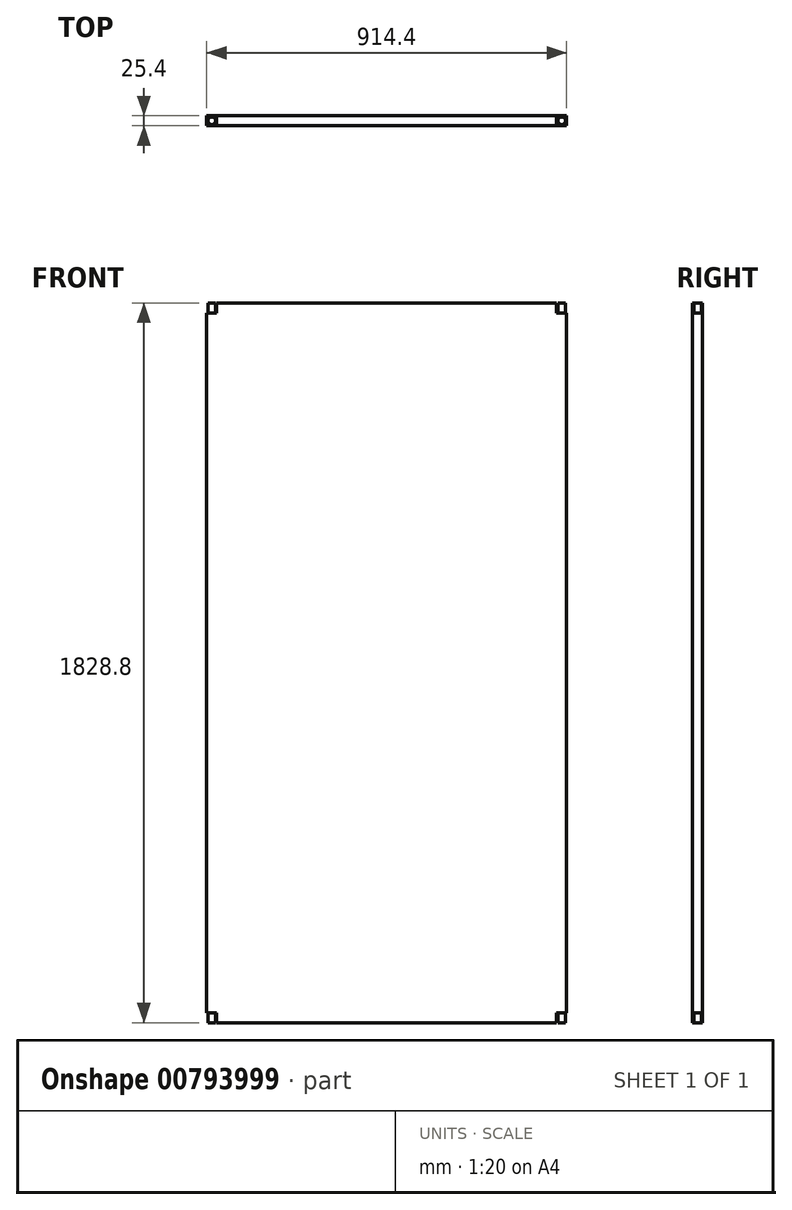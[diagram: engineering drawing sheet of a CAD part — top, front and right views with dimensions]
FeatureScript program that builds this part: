
annotation { "Feature Type Name" : "Feature", "Feature Type Description" : "" }
export const myFeature = defineFeature(function(context is Context, id is Id, definition is map)
    precondition{}
    {
        {
            var Q0;
            Q0=qCreatedBy(makeId("Front.planeOp"),FACE);
            var sketch = newSketch(context, id + "F0", { "sketchPlane" : qUnion([Q0])});
            skLineSegment(sketch, "E0.bottom", {"start": v(457.2, -914.4) * mm, "end": v(-457.2, -914.4) * mm});
            skLineSegment(sketch, "E0.top", {"start": v(457.2, 914.4) * mm, "end": v(-457.2, 914.4) * mm});
            skLineSegment(sketch, "E0.left", {"start": v(457.2, -914.4) * mm, "end": v(457.2, 914.4) * mm});
            skLineSegment(sketch, "E0.right", {"start": v(-457.2, -914.4) * mm, "end": v(-457.2, 914.4) * mm});
            skPoint(sketch, "E0.middle", {"position": v(0, 0) * mm});
            skSolve(sketch);
        }
        {
            var Q0;
            Q0 = qSketchRegion(id + "F0", true);
            extrude(context, id + "F1", {"entities" : qUnion([Q0]), "depth" : 25.4 * mm, "offsetDistance" : 25.4 * mm});
        }
        {
            var Q0;
            Q0=makeQuery(id+"F1.opExtrude","SWEPT_FACE",FACE,{"disambiguationData":[OSD([sQuery(id+"F0.wireOp",EDGE,"E0.top")])]});
            var sketch = newSketch(context, id + "F2", { "sketchPlane" : qUnion([Q0])});
            skLineSegment(sketch, "E1.bottom", {"start": v(-457.2, 0) * mm, "end": v(-431.8, 0) * mm});
            skLineSegment(sketch, "E1.top", {"start": v(-457.2, -25.4) * mm, "end": v(-431.8, -25.4) * mm});
            skLineSegment(sketch, "E1.left", {"start": v(-457.2, 0) * mm, "end": v(-457.2, -25.4) * mm});
            skLineSegment(sketch, "E1.right", {"start": v(-431.8, 0) * mm, "end": v(-431.8, -25.4) * mm});
            skLineSegment(sketch, "E2.bottom", {"start": v(457.2, 0) * mm, "end": v(431.8, 0) * mm});
            skLineSegment(sketch, "E2.top", {"start": v(457.2, -25.4) * mm, "end": v(431.8, -25.4) * mm});
            skLineSegment(sketch, "E2.left", {"start": v(457.2, 0) * mm, "end": v(457.2, -25.4) * mm});
            skLineSegment(sketch, "E2.right", {"start": v(431.8, 0) * mm, "end": v(431.8, -25.4) * mm});
            skLineSegment(sketch, "E3.left", {"start": v(-457.2, -25.4) * mm, "end": v(-457.2, 0) * mm});
            skLineSegment(sketch, "E3.right", {"start": v(-431.8, -25.4) * mm, "end": v(-431.8, 0) * mm});
            skSolve(sketch);
        }
        {
            var Q0;
            Q0 = qSketchRegion(id + "F2", true);
            extrude(context, id + "F3", {"entities" : qUnion([Q0]), "operationType" : NewBodyOperationType.REMOVE, "oppositeDirection" : true, "depth" : 25.4 * mm, "offsetDistance" : 25.4 * mm});
        }
        {
            var Q0;
            Q0=makeQuery(id+"F1.opExtrude","SWEPT_FACE",FACE,{"disambiguationData":[OSD([sQuery(id+"F0.wireOp",EDGE,"E0.bottom")])]});
            var sketch = newSketch(context, id + "F4", { "sketchPlane" : qUnion([Q0])});
            skLineSegment(sketch, "E4.bottom", {"start": v(-457.2, 25.4) * mm, "end": v(-431.8, 25.4) * mm});
            skLineSegment(sketch, "E4.top", {"start": v(-457.2, 0) * mm, "end": v(-431.8, 0) * mm});
            skLineSegment(sketch, "E4.left", {"start": v(-457.2, 25.4) * mm, "end": v(-457.2, 0) * mm});
            skLineSegment(sketch, "E4.right", {"start": v(-431.8, 25.4) * mm, "end": v(-431.8, 0) * mm});
            skLineSegment(sketch, "E5.bottom", {"start": v(457.2, 25.4) * mm, "end": v(431.8, 25.4) * mm});
            skLineSegment(sketch, "E5.top", {"start": v(457.2, 0) * mm, "end": v(431.8, 0) * mm});
            skLineSegment(sketch, "E5.left", {"start": v(457.2, 25.4) * mm, "end": v(457.2, 0) * mm});
            skLineSegment(sketch, "E5.right", {"start": v(431.8, 25.4) * mm, "end": v(431.8, 0) * mm});
            skSolve(sketch);
        }
        {
            var Q0;
            Q0 = qSketchRegion(id + "F4", true);
            extrude(context, id + "F5", {"entities" : qUnion([Q0]), "operationType" : NewBodyOperationType.REMOVE, "oppositeDirection" : true, "depth" : 25.4 * mm, "offsetDistance" : 25.4 * mm});
        }
        {
            var Q0;
            Q0=makeQuery(id+"F3.boolean.opBoolean","COPY",FACE,{"derivedFrom":makeQuery(id+"F3.opExtrude","CAP_FACE",FACE,{"disambiguationData":[OSD([sQuery(id+"F2.wireOp",EDGE,"E1.top"),sQuery(id+"F2.wireOp",EDGE,"E1.bottom"),sQuery(id+"F2.wireOp",EDGE,"E3.left"),sQuery(id+"F2.wireOp",EDGE,"E3.right")])],"isStart":false})});
            var sketch = newSketch(context, id + "F6", { "sketchPlane" : qUnion([Q0])});
            skPoint(sketch, "E6", {"position": v(-444.5, 0) * mm});
            skPoint(sketch, "E7", {"position": v(-457.2, -12.7) * mm});
            skCircle(sketch, "E8", {"center": v(-444.5, -12.7) * mm, "radius": 9.53 * mm});
            skSolve(sketch);
        }
        {
            var Q0;
            Q0 = qSketchRegion(id + "F6", true);
            extrude(context, id + "F7", {"entities" : qUnion([Q0]), "operationType" : NewBodyOperationType.ADD, "depth" : 25.4 * mm, "offsetDistance" : 25.4 * mm});
        }
        {
            var Q0;
            Q0=makeQuery(id+"F3.boolean.opBoolean","COPY",FACE,{"derivedFrom":makeQuery(id+"F3.opExtrude","CAP_FACE",FACE,{"disambiguationData":[OSD([sQuery(id+"F2.wireOp",EDGE,"E2.bottom"),sQuery(id+"F2.wireOp",EDGE,"E2.top"),sQuery(id+"F2.wireOp",EDGE,"E2.left"),sQuery(id+"F2.wireOp",EDGE,"E2.right")])],"isStart":false})});
            var sketch = newSketch(context, id + "F8", { "sketchPlane" : qUnion([Q0])});
            skPoint(sketch, "E9", {"position": v(444.5, 0) * mm});
            skPoint(sketch, "E10", {"position": v(457.2, -12.7) * mm});
            skCircle(sketch, "E11", {"center": v(444.5, -12.7) * mm, "radius": 9.53 * mm});
            skSolve(sketch);
        }
        {
            var Q0;
            Q0 = qSketchRegion(id + "F8", true);
            extrude(context, id + "F9", {"entities" : qUnion([Q0]), "operationType" : NewBodyOperationType.ADD, "depth" : 25.4 * mm, "offsetDistance" : 25.4 * mm});
        }
        {
            var Q0;
            Q0=makeQuery(id+"F5.boolean.opBoolean","COPY",FACE,{"derivedFrom":makeQuery(id+"F5.opExtrude","CAP_FACE",FACE,{"disambiguationData":[OSD([sQuery(id+"F4.wireOp",EDGE,"E4.bottom"),sQuery(id+"F4.wireOp",EDGE,"E4.top"),sQuery(id+"F4.wireOp",EDGE,"E4.left"),sQuery(id+"F4.wireOp",EDGE,"E4.right")])],"isStart":false})});
            var sketch = newSketch(context, id + "F10", { "sketchPlane" : qUnion([Q0])});
            skPoint(sketch, "E12", {"position": v(-444.5, 25.4) * mm});
            skPoint(sketch, "E13", {"position": v(-457.2, 12.7) * mm});
            skCircle(sketch, "E14", {"center": v(-444.5, 12.7) * mm, "radius": 9.53 * mm});
            skSolve(sketch);
        }
        {
            var Q0;
            Q0 = qSketchRegion(id + "F10", true);
            extrude(context, id + "F11", {"entities" : qUnion([Q0]), "operationType" : NewBodyOperationType.ADD, "depth" : 25.4 * mm, "offsetDistance" : 25.4 * mm});
        }
        {
            var Q0;
            Q0=makeQuery(id+"F5.boolean.opBoolean","COPY",FACE,{"derivedFrom":makeQuery(id+"F5.opExtrude","CAP_FACE",FACE,{"disambiguationData":[OSD([sQuery(id+"F4.wireOp",EDGE,"E5.bottom"),sQuery(id+"F4.wireOp",EDGE,"E5.top"),sQuery(id+"F4.wireOp",EDGE,"E5.left"),sQuery(id+"F4.wireOp",EDGE,"E5.right")])],"isStart":false})});
            var sketch = newSketch(context, id + "F12", { "sketchPlane" : qUnion([Q0])});
            skPoint(sketch, "E15", {"position": v(444.5, 25.4) * mm});
            skPoint(sketch, "E16", {"position": v(457.2, 12.7) * mm});
            skCircle(sketch, "E17", {"center": v(444.5, 12.7) * mm, "radius": 9.53 * mm});
            skSolve(sketch);
        }
        {
            var Q0;
            Q0 = qSketchRegion(id + "F12", true);
            extrude(context, id + "F13", {"entities" : qUnion([Q0]), "operationType" : NewBodyOperationType.ADD, "depth" : 25.4 * mm, "offsetDistance" : 25.4 * mm});
        }
    });
